# Revit family: 304_SM_4_1-_
name_source: partatom
category: Pipe Accessories
units: mm (PartAtom-declared; Revit-internal decimal feet)

## family parameters
Always vertical = Yes
Cut with Voids When Loaded = No
Part Type = Valve - Breaks Into
Round Connector Dimension = Use Diameter
Shared = No
Work Plane-Based = No

## types (2) — shared parameters
CAT0 = Yes
Description = SM - Dynamic Self Balancing Control Valve
H2 = 135 mm  [stored 0.442913 ft]
H3 = 270 mm  [stored 0.885827 ft]
L1 = 32 mm  [stored 0.104987 ft]
L1__ve = -32 mm  [stored -0.104987 ft]
L2 = 256 mm  [stored 0.839895 ft]
L2D = 320 mm
L2D_Min = 3048 mm  [stored 10 ft]
LL = 160 mm  [stored 0.524934 ft]
Manufacturer = FlowCon
QmdConnectorList = 301;D;302;D
R1 = 68 mm
URL = http://flowcon.com
magiPartTypeId = 304
magiProductFamilyId = SM.4.1-*
zero-valued in all types: MC_Default_elevation

## per-type parameters (varying)
| type | D | W2D | magiProductId |
| SM.4.1.B-80 | 80 mm | 80 mm  [stored 0.262467 ft] | SM.4.1-80 |
| SM.4.1.B-100 | 100 mm | 100 mm  [stored 0.328084 ft] | SM.4.1-100 |

note: column(s) folded — value = type name in every type: magiProductCode

note: [stored X ft] marks values corroborated as IEEE doubles in the binary element streams (Revit-internal decimal feet)

## geometry (parser evidence)
native form markers: Sweep x2
no freeform markers — native parametric forms only
